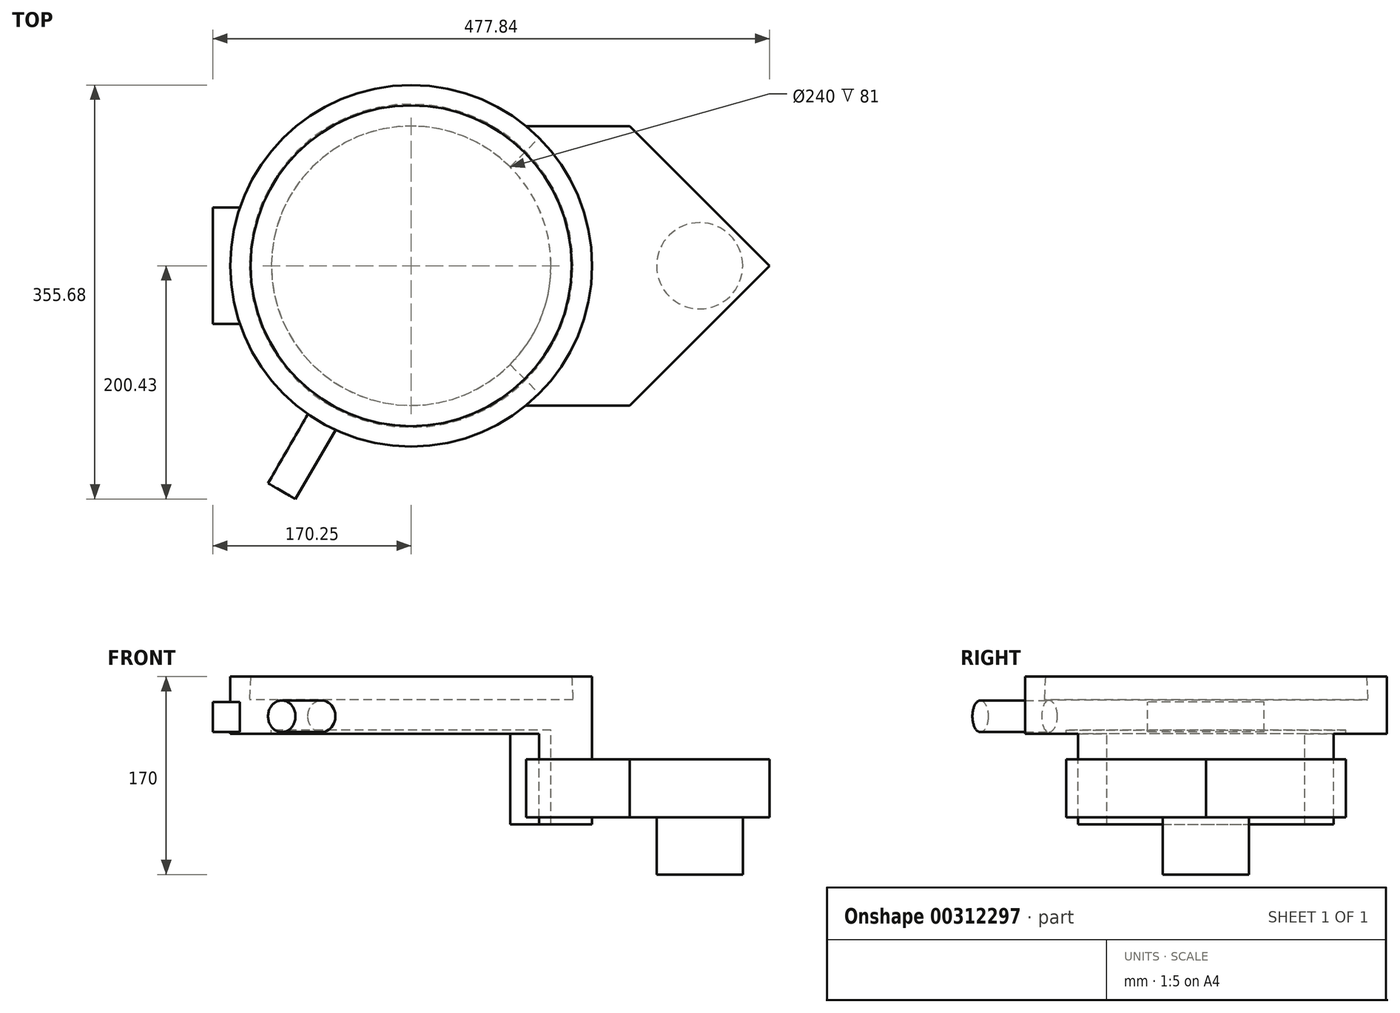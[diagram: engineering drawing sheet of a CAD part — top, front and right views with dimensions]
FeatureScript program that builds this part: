
annotation { "Feature Type Name" : "Feature", "Feature Type Description" : "" }
export const myFeature = defineFeature(function(context is Context, id is Id, definition is map)
    precondition{}
    {
        {
            var Q0;
            Q0=qCreatedBy(makeId("Top.planeOp"),FACE);
            var sketch = newSketch(context, id + "F0", { "sketchPlane" : qUnion([Q0])});
            skCircle(sketch, "E0", {"center": v(0, 0) * mm, "radius": 155.25 * mm});
            skCircle(sketch, "E1", {"center": v(0, 0) * mm, "radius": 120 * mm});
            skLineSegment(sketch, "E2", {"start": v(0, 0) * mm, "end": v(-155.25, 0) * mm});
            skCircle(sketch, "E3.cCircle", {"center": v(0, 0) * mm, "radius": 155.25 * mm, "construction": true});
            skLineSegment(sketch, "E4", {"start": v(0, 0) * mm, "end": v(109.78, -109.78) * mm});
            skLineSegment(sketch, "E5", {"start": v(0, 0) * mm, "end": v(109.78, 109.78) * mm});
            skArc(sketch, "E6", {"start": v(0, 155.25) * mm, "mid": v(-39.77, 150.07) * mm, "end": v(-76.89, 134.87) * mm});
            skCircle(sketch, "E7", {"center": v(0, 0) * mm, "radius": 137.8 * mm});
            skSolve(sketch);
        }
        {
            var Q0;
            Q0=makeQuery(id+"F0.imprint","IMPRINT",FACE,{"disambiguationData":[TD([[makeQuery(id+"F0.imprint","IMPRINT",EDGE,{"derivedFrom":sQuery(id+"F0.wireOp",EDGE,"SIjcpr7l-Zsjg-hIu2-9ESK-eZdlGyEDi106")}),-1.0]])]});
            var Q1;
            Q1=makeQuery(id+"F0.imprint","IMPRINT",FACE,{"disambiguationData":[TD([[makeQuery(id+"F0.imprint","IMPRINT",EDGE,{"derivedFrom":sQuery(id+"F0.wireOp",EDGE,"SIjcpr7l-Zsjg-hIu2-9ESK-eZdlGyEDi106")}),1.0]])]});
            var Q2;
            Q2=makeQuery(id+"F0.imprint","IMPRINT",FACE,{"disambiguationData":[TD([[makeQuery(id+"F0.imprint","IMPRINT",EDGE,{"derivedFrom":sQuery(id+"F0.wireOp",EDGE,"E1")}),1.0]])]});
            var Q3;
            {var subQ0=sQuery(id+"F0.wireOp",EDGE,"E2");var subQ1=sQuery(id+"F0.wireOp",EDGE,"E0");var subQ2=makeQuery(id+"F0.imprint","INTERSECT",VERTEX,{"derivedFrom":[subQ1,subQ0]});Q3=makeQuery(id+"F0.imprint","IMPRINT",FACE,{"disambiguationData":[TD([[makeQuery(id+"F0.imprint","IMPRINT",EDGE,{"disambiguationData":[TD([[subQ2,1.0]])],"derivedFrom":subQ1}),1.0]])]});}
            var Q4;
            {var subQ0=sQuery(id+"F0.wireOp",EDGE,"E2");var subQ1=sQuery(id+"F0.wireOp",EDGE,"E0");var subQ2=makeQuery(id+"F0.imprint","INTERSECT",VERTEX,{"derivedFrom":[subQ1,subQ0]});Q4=makeQuery(id+"F0.imprint","IMPRINT",FACE,{"disambiguationData":[TD([[makeQuery(id+"F0.imprint","IMPRINT",EDGE,{"disambiguationData":[TD([[subQ2,-1.0]])],"derivedFrom":subQ1}),1.0]])]});}
            var Q5;
            {var subQ0=sQuery(id+"F0.wireOp",EDGE,"E4");var subQ1=sQuery(id+"F0.wireOp",EDGE,"E0");var subQ2=makeQuery(id+"F0.imprint","INTERSECT",VERTEX,{"derivedFrom":[subQ1,subQ0]});Q5=makeQuery(id+"F0.imprint","IMPRINT",FACE,{"disambiguationData":[TD([[makeQuery(id+"F0.imprint","IMPRINT",EDGE,{"disambiguationData":[TD([[subQ2,-1.0]])],"derivedFrom":subQ1}),1.0]])]});}
            var Q6;
            {var subQ0=sQuery(id+"F0.wireOp",EDGE,"E2");var subQ1=sQuery(id+"F0.wireOp",EDGE,"E1");var subQ2=makeQuery(id+"F0.imprint","INTERSECT",VERTEX,{"derivedFrom":[subQ1,subQ0]});Q6=makeQuery(id+"F0.imprint","IMPRINT",FACE,{"disambiguationData":[TD([[makeQuery(id+"F0.imprint","IMPRINT",EDGE,{"disambiguationData":[TD([[subQ2,-1.0]])],"derivedFrom":subQ1}),-1.0]])]});}
            var Q7;
            {var subQ0=sQuery(id+"F0.wireOp",EDGE,"E2");var subQ1=sQuery(id+"F0.wireOp",EDGE,"E1");var subQ2=makeQuery(id+"F0.imprint","INTERSECT",VERTEX,{"derivedFrom":[subQ1,subQ0]});Q7=makeQuery(id+"F0.imprint","IMPRINT",FACE,{"disambiguationData":[TD([[makeQuery(id+"F0.imprint","IMPRINT",EDGE,{"disambiguationData":[TD([[subQ2,1.0]])],"derivedFrom":subQ1}),-1.0]])]});}
            var Q8;
            {var subQ0=sQuery(id+"F0.wireOp",EDGE,"E5");var subQ1=sQuery(id+"F0.wireOp",EDGE,"E1");var subQ2=makeQuery(id+"F0.imprint","INTERSECT",VERTEX,{"derivedFrom":[subQ1,subQ0]});Q8=makeQuery(id+"F0.imprint","IMPRINT",FACE,{"disambiguationData":[TD([[makeQuery(id+"F0.imprint","IMPRINT",EDGE,{"disambiguationData":[TD([[subQ2,1.0]])],"derivedFrom":subQ1}),-1.0]])]});}
            extrude(context, id + "F1", {"entities" : qUnion([Q0, Q1, Q2, Q3, Q4, Q5, Q6, Q7, Q8]), "oppositeDirection" : true, "depth" : 49 * mm});
        }
        {
            var Q0;
            {var subQ0=sQuery(id+"F0.wireOp",EDGE,"E2");var subQ1=sQuery(id+"F0.wireOp",EDGE,"E1");var subQ2=makeQuery(id+"F0.imprint","INTERSECT",VERTEX,{"derivedFrom":[subQ1,subQ0]});Q0=makeQuery(id+"F0.imprint","IMPRINT",FACE,{"disambiguationData":[TD([[makeQuery(id+"F0.imprint","IMPRINT",EDGE,{"disambiguationData":[TD([[subQ2,1.0]])],"derivedFrom":subQ1}),1.0]])]});}
            var Q1;
            {var subQ0=sQuery(id+"F0.wireOp",EDGE,"E5");var subQ1=sQuery(id+"F0.wireOp",EDGE,"E1");var subQ2=makeQuery(id+"F0.imprint","INTERSECT",VERTEX,{"derivedFrom":[subQ1,subQ0]});Q1=makeQuery(id+"F0.imprint","IMPRINT",FACE,{"disambiguationData":[TD([[makeQuery(id+"F0.imprint","IMPRINT",EDGE,{"disambiguationData":[TD([[subQ2,1.0]])],"derivedFrom":subQ1}),1.0]])]});}
            var Q2;
            {var subQ0=sQuery(id+"F0.wireOp",EDGE,"E2");var subQ1=sQuery(id+"F0.wireOp",EDGE,"E1");var subQ2=makeQuery(id+"F0.imprint","INTERSECT",VERTEX,{"derivedFrom":[subQ1,subQ0]});Q2=makeQuery(id+"F0.imprint","IMPRINT",FACE,{"disambiguationData":[TD([[makeQuery(id+"F0.imprint","IMPRINT",EDGE,{"disambiguationData":[TD([[subQ2,-1.0]])],"derivedFrom":subQ1}),-1.0]])]});}
            var Q3;
            {var subQ0=sQuery(id+"F0.wireOp",EDGE,"E2");var subQ1=sQuery(id+"F0.wireOp",EDGE,"E1");var subQ2=makeQuery(id+"F0.imprint","INTERSECT",VERTEX,{"derivedFrom":[subQ1,subQ0]});Q3=makeQuery(id+"F0.imprint","IMPRINT",FACE,{"disambiguationData":[TD([[makeQuery(id+"F0.imprint","IMPRINT",EDGE,{"disambiguationData":[TD([[subQ2,1.0]])],"derivedFrom":subQ1}),-1.0]])]});}
            var Q4;
            {var subQ0=sQuery(id+"F0.wireOp",EDGE,"E5");var subQ1=sQuery(id+"F0.wireOp",EDGE,"E1");var subQ2=makeQuery(id+"F0.imprint","INTERSECT",VERTEX,{"derivedFrom":[subQ1,subQ0]});Q4=makeQuery(id+"F0.imprint","IMPRINT",FACE,{"disambiguationData":[TD([[makeQuery(id+"F0.imprint","IMPRINT",EDGE,{"disambiguationData":[TD([[subQ2,1.0]])],"derivedFrom":subQ1}),-1.0]])]});}
            var Q5;
            {var subQ0=sQuery(id+"F0.wireOp",EDGE,"E2");var subQ1=sQuery(id+"F0.wireOp",EDGE,"E1");var subQ2=makeQuery(id+"F0.imprint","INTERSECT",VERTEX,{"derivedFrom":[subQ1,subQ0]});Q5=makeQuery(id+"F0.imprint","IMPRINT",FACE,{"disambiguationData":[TD([[makeQuery(id+"F0.imprint","IMPRINT",EDGE,{"disambiguationData":[TD([[subQ2,-1.0]])],"derivedFrom":subQ1}),1.0]])]});}
            extrude(context, id + "F2", {"entities" : qUnion([Q0, Q1, Q2, Q3, Q4, Q5]), "operationType" : NewBodyOperationType.REMOVE, "oppositeDirection" : true, "depth" : 20 * mm, "hasDraft" : true, "draftAngle" : 3 * degree});
        }
        {
            var Q0;
            {var subQ0=sQuery(id+"F0.wireOp",EDGE,"E2");var subQ1=sQuery(id+"F0.wireOp",EDGE,"E1");var subQ2=makeQuery(id+"F0.imprint","INTERSECT",VERTEX,{"derivedFrom":[subQ1,subQ0]});Q0=makeQuery(id+"F0.imprint","IMPRINT",FACE,{"disambiguationData":[TD([[makeQuery(id+"F0.imprint","IMPRINT",EDGE,{"disambiguationData":[TD([[subQ2,-1.0]])],"derivedFrom":subQ1}),1.0]])]});}
            var Q1;
            {var subQ0=sQuery(id+"F0.wireOp",EDGE,"E2");var subQ1=sQuery(id+"F0.wireOp",EDGE,"E1");var subQ2=makeQuery(id+"F0.imprint","INTERSECT",VERTEX,{"derivedFrom":[subQ1,subQ0]});Q1=makeQuery(id+"F0.imprint","IMPRINT",FACE,{"disambiguationData":[TD([[makeQuery(id+"F0.imprint","IMPRINT",EDGE,{"disambiguationData":[TD([[subQ2,1.0]])],"derivedFrom":subQ1}),1.0]])]});}
            var Q2;
            {var subQ0=sQuery(id+"F0.wireOp",EDGE,"E5");var subQ1=sQuery(id+"F0.wireOp",EDGE,"E1");var subQ2=makeQuery(id+"F0.imprint","INTERSECT",VERTEX,{"derivedFrom":[subQ1,subQ0]});Q2=makeQuery(id+"F0.imprint","IMPRINT",FACE,{"disambiguationData":[TD([[makeQuery(id+"F0.imprint","IMPRINT",EDGE,{"disambiguationData":[TD([[subQ2,1.0]])],"derivedFrom":subQ1}),1.0]])]});}
            extrude(context, id + "F3", {"entities" : qUnion([Q0, Q1, Q2]), "operationType" : NewBodyOperationType.REMOVE, "oppositeDirection" : true, "depth" : 49 * mm, "hasSecondDirection" : true, "secondDirectionOppositeDirection" : true, "secondDirectionDepth" : 46 * mm});
        }
        {
            var Q0;
            {var subQ0=sQuery(id+"F0.wireOp",EDGE,"E5");var subQ1=sQuery(id+"F0.wireOp",EDGE,"E1");var subQ2=makeQuery(id+"F0.imprint","INTERSECT",VERTEX,{"derivedFrom":[subQ1,subQ0]});Q0=makeQuery(id+"F0.imprint","IMPRINT",FACE,{"disambiguationData":[TD([[makeQuery(id+"F0.imprint","IMPRINT",EDGE,{"disambiguationData":[TD([[subQ2,1.0]])],"derivedFrom":subQ1}),-1.0]])]});}
            var Q1;
            {var subQ0=sQuery(id+"F0.wireOp",EDGE,"E4");var subQ1=sQuery(id+"F0.wireOp",EDGE,"E0");var subQ2=makeQuery(id+"F0.imprint","INTERSECT",VERTEX,{"derivedFrom":[subQ1,subQ0]});Q1=makeQuery(id+"F0.imprint","IMPRINT",FACE,{"disambiguationData":[TD([[makeQuery(id+"F0.imprint","IMPRINT",EDGE,{"disambiguationData":[TD([[subQ2,-1.0]])],"derivedFrom":subQ1}),1.0]])]});}
            extrude(context, id + "F4", {"entities" : qUnion([Q0, Q1]), "operationType" : NewBodyOperationType.ADD, "oppositeDirection" : true, "depth" : 127 * mm, "hasSecondDirection" : true, "secondDirectionOppositeDirection" : true, "secondDirectionDepth" : 49 * mm});
        }
        {
            var Q0;
            {var subQ0=sQuery(id+"F0.wireOp",EDGE,"E2");var subQ1=sQuery(id+"F0.wireOp",EDGE,"E1");var subQ2=makeQuery(id+"F0.imprint","INTERSECT",VERTEX,{"derivedFrom":[subQ1,subQ0]});Q0=makeQuery(id+"F0.imprint","IMPRINT",FACE,{"disambiguationData":[TD([[makeQuery(id+"F0.imprint","IMPRINT",EDGE,{"disambiguationData":[TD([[subQ2,-1.0]])],"derivedFrom":subQ1}),1.0]])]});}
            var sketch = newSketch(context, id + "F5", { "sketchPlane" : qUnion([Q0])});
            skLineSegment(sketch, "E8", {"start": v(0, 155.25) * mm, "end": v(0, -155.25) * mm});
            skCircle(sketch, "E9.cCircle", {"center": v(0, 0) * mm, "radius": 155.25 * mm, "construction": true});
            skLineSegment(sketch, "E9.0", {"start": v(0, -155.25) * mm, "end": v(-77.62, -134.45) * mm});
            skLineSegment(sketch, "E9.1", {"start": v(-77.62, -134.45) * mm, "end": v(-134.45, -77.63) * mm});
            skLineSegment(sketch, "E9.2", {"start": v(-134.45, -77.63) * mm, "end": v(-155.25, 0) * mm});
            skLineSegment(sketch, "E9.3", {"start": v(-155.25, 0) * mm, "end": v(-134.45, 77.62) * mm});
            skLineSegment(sketch, "E9.4", {"start": v(-134.45, 77.62) * mm, "end": v(-77.63, 134.45) * mm});
            skLineSegment(sketch, "E9.5", {"start": v(-77.63, 134.45) * mm, "end": v(0, 155.25) * mm});
            skLineSegment(sketch, "E9.6", {"start": v(0, 155.25) * mm, "end": v(77.62, 134.45) * mm});
            skLineSegment(sketch, "E9.7", {"start": v(77.62, 134.45) * mm, "end": v(134.45, 77.63) * mm});
            skLineSegment(sketch, "E9.8", {"start": v(134.45, 77.63) * mm, "end": v(155.25, 0) * mm});
            skLineSegment(sketch, "E9.9", {"start": v(155.25, 0) * mm, "end": v(134.45, -77.62) * mm});
            skLineSegment(sketch, "E9.10", {"start": v(134.45, -77.62) * mm, "end": v(77.63, -134.45) * mm});
            skLineSegment(sketch, "E9.11", {"start": v(77.62, -134.45) * mm, "end": v(0, -155.25) * mm});
            skLineSegment(sketch, "E10", {"start": v(0, 0) * mm, "end": v(-77.62, -134.45) * mm});
            skLineSegment(sketch, "E11", {"start": v(0, 0) * mm, "end": v(-77.63, 134.45) * mm});
            skLineSegment(sketch, "E12", {"start": v(187.59, 0) * mm, "end": v(187.59, 120) * mm});
            skLineSegment(sketch, "E13", {"start": v(187.59, 120) * mm, "end": v(98.5, 120) * mm});
            skLineSegment(sketch, "E14", {"start": v(187.59, 0) * mm, "end": v(187.59, -120) * mm});
            skLineSegment(sketch, "E15", {"start": v(187.59, -120) * mm, "end": v(98.5, -120) * mm});
            skLineSegment(sketch, "E16", {"start": v(98.5, 120) * mm, "end": v(0, 0) * mm});
            skLineSegment(sketch, "E17", {"start": v(98.5, -120) * mm, "end": v(0, 0) * mm});
            skLineSegment(sketch, "E18", {"start": v(187.59, 0) * mm, "end": v(307.59, 0) * mm});
            skLineSegment(sketch, "E19", {"start": v(307.59, 0) * mm, "end": v(187.59, -120) * mm});
            skLineSegment(sketch, "E20.MirrorCS", {"start": v(307.59, 0) * mm, "end": v(187.59, 120) * mm});
            skCircle(sketch, "E21", {"center": v(247.59, 0) * mm, "radius": 37 * mm});
            skCircle(sketch, "E22", {"center": v(0, 0) * mm, "radius": 155.25 * mm});
            skLineSegment(sketch, "E23", {"start": v(-77.62, -134.45) * mm, "end": v(36.6, -200.4) * mm});
            skLineSegment(sketch, "E24.bottom", {"start": v(-155.25, 0) * mm, "end": v(-134.25, 0) * mm});
            skLineSegment(sketch, "E24.top", {"start": v(-155.25, -35) * mm, "end": v(-134.25, -35) * mm});
            skLineSegment(sketch, "E24.left", {"start": v(-155.25, 0) * mm, "end": v(-155.25, -35) * mm});
            skLineSegment(sketch, "E24.right", {"start": v(-134.25, 0) * mm, "end": v(-134.25, -35) * mm});
            skLineSegment(sketch, "E25.bottom", {"start": v(-155.25, 0) * mm, "end": v(-170.25, 0) * mm});
            skLineSegment(sketch, "E25.top", {"start": v(-155.25, -35) * mm, "end": v(-170.25, -35) * mm});
            skLineSegment(sketch, "E25.right", {"start": v(-170.25, 0) * mm, "end": v(-170.25, -35) * mm});
            skLineSegment(sketch, "E26.MirrorCS", {"start": v(-134.25, 0) * mm, "end": v(-134.25, 35) * mm});
            skLineSegment(sketch, "E27.MirrorCS", {"start": v(-170.25, 0) * mm, "end": v(-170.25, 35) * mm});
            skLineSegment(sketch, "E28.MirrorCS", {"start": v(-155.25, 35) * mm, "end": v(-170.25, 35) * mm});
            skLineSegment(sketch, "E29.MirrorCS", {"start": v(-155.25, 0) * mm, "end": v(-155.25, 35) * mm});
            skLineSegment(sketch, "E30.MirrorCS", {"start": v(-155.25, 35) * mm, "end": v(-134.25, 35) * mm});
            skLineSegment(sketch, "E31", {"start": v(-155.25, 0) * mm, "end": v(-155.25, 50) * mm});
            skLineSegment(sketch, "E32", {"start": v(-155.25, 50) * mm, "end": v(-117.25, 50) * mm});
            skLineSegment(sketch, "E33", {"start": v(-117.25, 50) * mm, "end": v(-117.25, 0) * mm});
            skLineSegment(sketch, "E34", {"start": v(-170.25, 0) * mm, "end": v(-170.25, 50) * mm});
            skLineSegment(sketch, "E35", {"start": v(-170.25, 50) * mm, "end": v(-155.25, 50) * mm});
            skLineSegment(sketch, "E36.MirrorCS", {"start": v(-170.25, 0) * mm, "end": v(-170.25, -50) * mm});
            skLineSegment(sketch, "E37.MirrorCS", {"start": v(-170.25, -50) * mm, "end": v(-155.25, -50) * mm});
            skLineSegment(sketch, "E38.MirrorCS", {"start": v(-155.25, -50) * mm, "end": v(-117.25, -50) * mm});
            skLineSegment(sketch, "E39.MirrorCS", {"start": v(-117.25, -50) * mm, "end": v(-117.25, 0) * mm});
            skSolve(sketch);
        }
        {
            var Q0;
            Q0=makeQuery(id+"F5.imprint","IMPRINT",FACE,{"disambiguationData":[TD([[makeQuery(id+"F5.imprint","IMPRINT",EDGE,{"derivedFrom":sQuery(id+"F5.wireOp",EDGE,"E12")}),1.0]])]});
            var Q1;
            {var subQ4=sQuery(id+"F5.wireOp",EDGE,"E14");Q1=makeQuery(id+"F5.imprint","IMPRINT",FACE,{"disambiguationData":[TD([[makeQuery(id+"F5.imprint","IMPRINT",EDGE,{"derivedFrom":subQ4}),1.0]])]});}
            var Q2;
            {var subQ4=sQuery(id+"F5.wireOp",EDGE,"E12");Q2=makeQuery(id+"F5.imprint","IMPRINT",FACE,{"disambiguationData":[TD([[makeQuery(id+"F5.imprint","IMPRINT",EDGE,{"derivedFrom":subQ4}),-1.0]])]});}
            var Q3;
            {var subQ0=sQuery(id+"F5.wireOp",EDGE,"E21");var subQ1=sQuery(id+"F5.wireOp",EDGE,"E18");var subQ2=makeQuery(id+"F5.imprint","INTERSECT",VERTEX,{"disambiguationData":[OD(0.0)],"derivedFrom":[subQ1,subQ0]});Q3=makeQuery(id+"F5.imprint","IMPRINT",FACE,{"disambiguationData":[TD([[makeQuery(id+"F5.imprint","IMPRINT",EDGE,{"disambiguationData":[TD([[subQ2,-1.0]])],"derivedFrom":subQ1}),1.0]])]});}
            var Q4;
            {var subQ0=sQuery(id+"F5.wireOp",EDGE,"E21");var subQ1=sQuery(id+"F5.wireOp",EDGE,"E18");var subQ2=makeQuery(id+"F5.imprint","INTERSECT",VERTEX,{"disambiguationData":[OD(0.0)],"derivedFrom":[subQ1,subQ0]});Q4=makeQuery(id+"F5.imprint","IMPRINT",FACE,{"disambiguationData":[TD([[makeQuery(id+"F5.imprint","IMPRINT",EDGE,{"disambiguationData":[TD([[subQ2,-1.0]])],"derivedFrom":subQ1}),-1.0]])]});}
            extrude(context, id + "F6", {"entities" : qUnion([Q0, Q1, Q2, Q3, Q4]), "operationType" : NewBodyOperationType.ADD, "oppositeDirection" : true, "depth" : 121 * mm, "hasSecondDirection" : true, "secondDirectionOppositeDirection" : true, "secondDirectionDepth" : 71 * mm});
        }
        {
            var Q0;
            {var subQ0=sQuery(id+"F5.wireOp",EDGE,"E21");var subQ1=sQuery(id+"F5.wireOp",EDGE,"E18");var subQ2=makeQuery(id+"F5.imprint","INTERSECT",VERTEX,{"disambiguationData":[OD(0.0)],"derivedFrom":[subQ1,subQ0]});Q0=makeQuery(id+"F5.imprint","IMPRINT",FACE,{"disambiguationData":[TD([[makeQuery(id+"F5.imprint","IMPRINT",EDGE,{"disambiguationData":[TD([[subQ2,-1.0]])],"derivedFrom":subQ1}),-1.0]])]});}
            var Q1;
            {var subQ0=sQuery(id+"F5.wireOp",EDGE,"E21");var subQ1=sQuery(id+"F5.wireOp",EDGE,"E18");var subQ2=makeQuery(id+"F5.imprint","INTERSECT",VERTEX,{"disambiguationData":[OD(0.0)],"derivedFrom":[subQ1,subQ0]});Q1=makeQuery(id+"F5.imprint","IMPRINT",FACE,{"disambiguationData":[TD([[makeQuery(id+"F5.imprint","IMPRINT",EDGE,{"disambiguationData":[TD([[subQ2,-1.0]])],"derivedFrom":subQ1}),1.0]])]});}
            extrude(context, id + "F7", {"entities" : qUnion([Q0, Q1]), "operationType" : NewBodyOperationType.ADD, "oppositeDirection" : true, "depth" : 170 * mm, "hasSecondDirection" : true, "secondDirectionOppositeDirection" : true, "secondDirectionDepth" : 119 * mm});
        }
        {
            var Q0;
            Q0=sQuery(id+"F5.wireOp",VERTEX,"E10.end");
            var Q1;
            Q1=sQuery(id+"F5.wireOp",EDGE,"E10");
            cPlane(context, id + "F8", {"entities" : qUnion([Q0, Q1]), "cplaneType" : CPlaneType.CURVE_POINT, "offset" : 25 * mm, "width" : 150 * mm, "height" : 150 * mm});
        }
        {
            var Q0;
            Q0=qCreatedBy(id+"F8.planeOp",FACE);
            var sketch = newSketch(context, id + "F9", { "sketchPlane" : qUnion([Q0])});
            skCircle(sketch, "E40", {"center": v(0.59, -34.09) * mm, "radius": 13.6 * mm});
            skSolve(sketch);
        }
        {
            var Q0;
            Q0 = qSketchRegion(id + "F9", true);
            extrude(context, id + "F10", {"entities" : qUnion([Q0]), "operationType" : NewBodyOperationType.ADD, "depth" : 68 * mm, "hasSecondDirection" : true, "secondDirectionOppositeDirection" : true, "secondDirectionDepth" : 2 * mm});
        }
        {
            var Q0;
            {var subQ1=sQuery(id+"F5.wireOp",EDGE,"E25.top");Q0=makeQuery(id+"F5.imprint","IMPRINT",FACE,{"disambiguationData":[TD([[makeQuery(id+"F5.imprint","IMPRINT",EDGE,{"derivedFrom":subQ1}),1.0]])]});}
            var Q1;
            {var subQ0=sQuery(id+"F5.wireOp",EDGE,"E25.top");Q1=makeQuery(id+"F5.imprint","IMPRINT",FACE,{"disambiguationData":[TD([[makeQuery(id+"F5.imprint","IMPRINT",EDGE,{"derivedFrom":subQ0}),-1.0]])]});}
            var Q2;
            {var subQ0=sQuery(id+"F5.wireOp",EDGE,"E24.left");Q2=makeQuery(id+"F5.imprint","IMPRINT",FACE,{"disambiguationData":[TD([[makeQuery(id+"F5.imprint","IMPRINT",EDGE,{"derivedFrom":subQ0}),1.0]])]});}
            var Q3;
            {var subQ0=sQuery(id+"F5.wireOp",EDGE,"E25.bottom");Q3=makeQuery(id+"F5.imprint","IMPRINT",FACE,{"disambiguationData":[TD([[makeQuery(id+"F5.imprint","IMPRINT",EDGE,{"derivedFrom":subQ0}),-1.0]])]});}
            var Q4;
            {var subQ1=sQuery(id+"F5.wireOp",EDGE,"E22");var subQ3=sQuery(id+"F5.wireOp",EDGE,"E30.MirrorCS");var subQ4=makeQuery(id+"F5.imprint","INTERSECT",VERTEX,{"derivedFrom":[subQ1,subQ3]});Q4=makeQuery(id+"F5.imprint","IMPRINT",FACE,{"disambiguationData":[TD([[makeQuery(id+"F5.imprint","IMPRINT",EDGE,{"disambiguationData":[TD([[subQ4,1.0]])],"derivedFrom":subQ3}),-1.0]])]});}
            var Q5;
            {var subQ0=sQuery(id+"F5.wireOp",EDGE,"E32");var subQ1=sQuery(id+"F5.wireOp",EDGE,"E22");var subQ2=makeQuery(id+"F5.imprint","INTERSECT",VERTEX,{"derivedFrom":[subQ1,subQ0]});Q5=makeQuery(id+"F5.imprint","IMPRINT",FACE,{"disambiguationData":[TD([[makeQuery(id+"F5.imprint","IMPRINT",EDGE,{"disambiguationData":[TD([[subQ2,-1.0]])],"derivedFrom":subQ1}),-1.0]])]});}
            var Q6;
            {var subQ0=sQuery(id+"F5.wireOp",EDGE,"E28.MirrorCS");Q6=makeQuery(id+"F5.imprint","IMPRINT",FACE,{"disambiguationData":[TD([[makeQuery(id+"F5.imprint","IMPRINT",EDGE,{"derivedFrom":subQ0}),-1.0]])]});}
            extrude(context, id + "F11", {"entities" : qUnion([Q0, Q1, Q2, Q3, Q4, Q5, Q6]), "operationType" : NewBodyOperationType.ADD, "oppositeDirection" : true, "depth" : 47.7 * mm, "hasSecondDirection" : true, "secondDirectionOppositeDirection" : true, "secondDirectionDepth" : 21.9 * mm});
        }
    });
